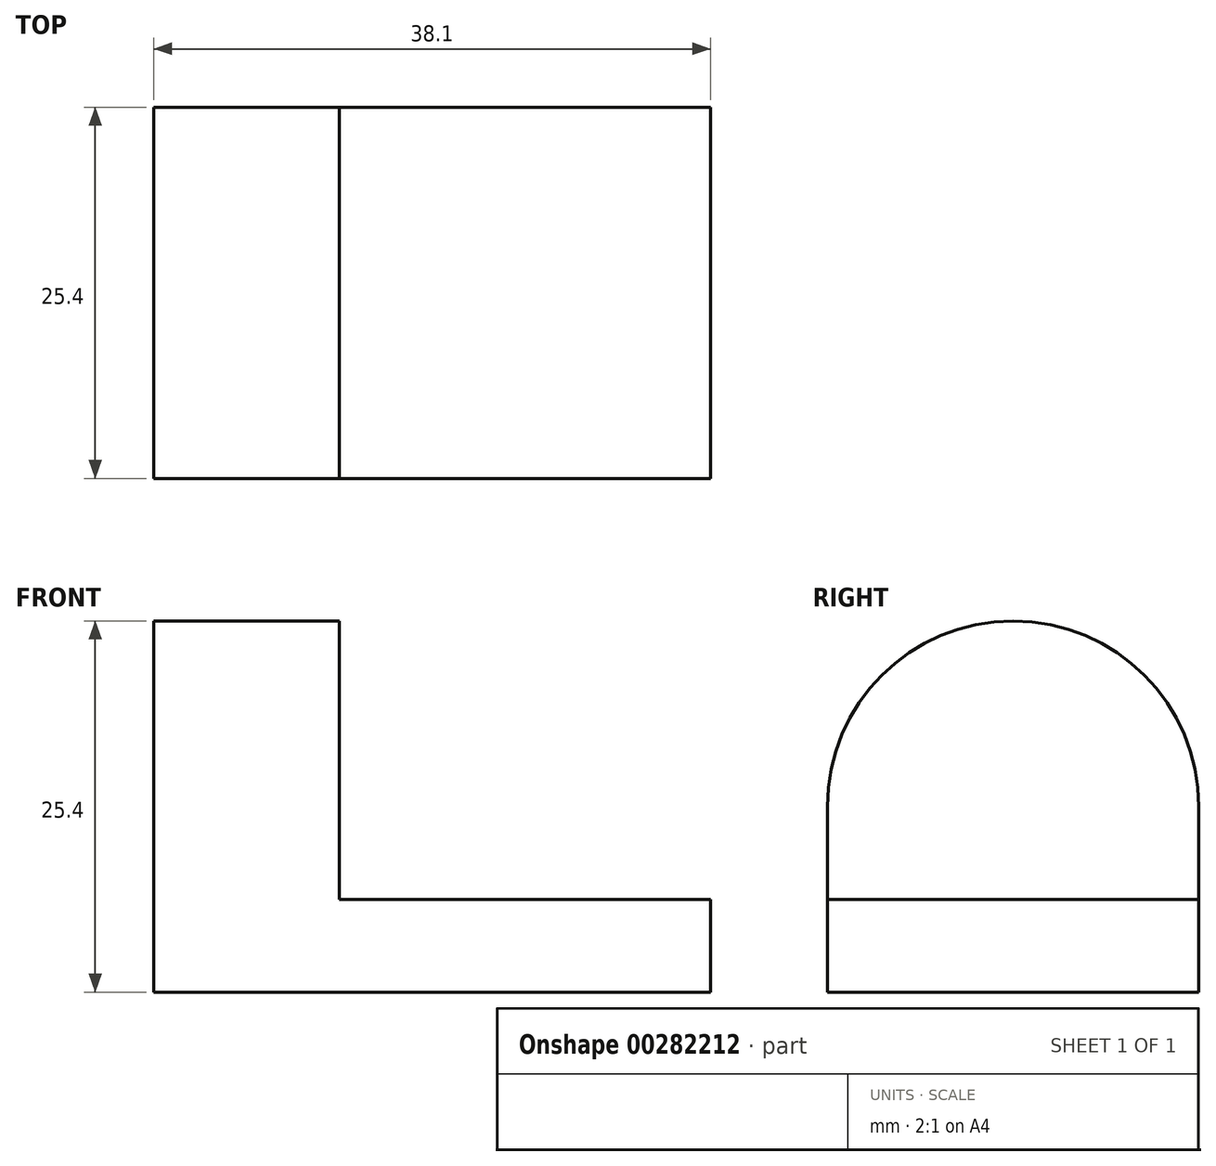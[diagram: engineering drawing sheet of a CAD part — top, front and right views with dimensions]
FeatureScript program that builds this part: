
annotation { "Feature Type Name" : "Feature", "Feature Type Description" : "" }
export const myFeature = defineFeature(function(context is Context, id is Id, definition is map)
    precondition{}
    {
        {
            var Q0;
            Q0=qCreatedBy(makeId("Top.planeOp"),FACE);
            var sketch = newSketch(context, id + "F0", { "sketchPlane" : qUnion([Q0])});
            skLineSegment(sketch, "E0", {"start": v(0, 0) * mm, "end": v(0, -25.4) * mm});
            skLineSegment(sketch, "E1", {"start": v(0, -25.4) * mm, "end": v(38.1, -25.4) * mm});
            skLineSegment(sketch, "E2", {"start": v(38.1, -25.4) * mm, "end": v(38.1, 0) * mm});
            skLineSegment(sketch, "E3", {"start": v(38.1, 0) * mm, "end": v(0, 0) * mm});
            skSolve(sketch);
        }
        {
            var Q0;
            Q0 = qSketchRegion(id + "F0", true);
            extrude(context, id + "F1", {"entities" : qUnion([Q0]), "depth" : 6.35 * mm});
        }
        {
            var Q0;
            Q0=qCreatedBy(makeId("Right.planeOp"),FACE);
            var sketch = newSketch(context, id + "F2", { "sketchPlane" : qUnion([Q0])});
            skLineSegment(sketch, "E4", {"start": v(0, 6.35) * mm, "end": v(-25.4, 6.35) * mm});
            skLineSegment(sketch, "E5", {"start": v(-25.4, 6.35) * mm, "end": v(-25.4, 12.7) * mm});
            skLineSegment(sketch, "E6", {"start": v(0, 12.7) * mm, "end": v(0, 6.35) * mm});
            skArc(sketch, "E7", {"start": v(0, 12.7) * mm, "mid": v(-12.7, 25.4) * mm, "end": v(-25.4, 12.7) * mm});
            skSolve(sketch);
        }
        {
            var Q0;
            Q0=makeQuery(id+"F2.imprint","IMPRINT",FACE,{"disambiguationData":[TD([[makeQuery(id+"F2.imprint","IMPRINT",EDGE,{"derivedFrom":sQuery(id+"F2.wireOp",EDGE,"E4")}),-1.0]])]});
            extrude(context, id + "F3", {"entities" : qUnion([Q0]), "operationType" : NewBodyOperationType.ADD, "depth" : 12.7 * mm});
        }
    });
